# Revit family: Grohe_PlumbingFixture_Essentials_TowelRail_40366001a
name_source: partatom
category: Plumbing Fixtures
revit_build: Autodesk Revit 2018 (Build: 20190510_1515(x64)
units: mm (PartAtom-declared; Revit-internal decimal feet)

## family parameters
Cut with Voids When Loaded = No
Host = Face
OmniClass Number = 23.65.00.00
OmniClass Title = Supply and Distribution of Liquids and Gases
Part Type = Normal
Room Calculation Point = No
Round Connector Dimension = Use Diameter
Shared = No

## types (1)
- 40366001
    ADACompliant = No
    Assembly Code = D2010
    AssetType = Fixed
    BIMObjectName = Grohe_PlumbingFixture_Essentials_TowelRail_40366001
    CWFU = 0
    ClassificationName = Uniclass 2015
    ClassificationValue = Pr_40_20_76_90
    ColdWaterConnectionDiameter = 10 mm  [stored 0.0328084 ft]
    Color = Chrome
    Cost = 0 $
    Default Elevation = 0 mm  [stored 0 ft]
    Description = To create your very own bathroom design blending harmonious style and user-friendly functionality has never been easier. Simply add a choice of our beautifully crafted GROHE Essentials accessories such as the slim yet sturdy 600mm towel rail – the perfect place to hang a bathroom towel. The rail has concealed fastenings and a durable, easy-care GROHE StarLight chrome finish that will sparkle for years. It’s also easy to fit – just follow the clear step-by-step instructions. Don’t forget to check out other products in the comprehensive collection such as the robe hook, toilet brush set, toilet paper holder and numerous towel rails and bath grips. Or for added ease and convenience why not try one of our complementary all-in-one sets? GROHE Essentials accessories – precision craftsmanship, highest quality materials and design that lasts!
    DocumentationCertificates = www.grohe.co.uk/
    DocumentationInstallationGuide = www.grohe.co.uk/
    DocumentationLiterature = www.grohe.co.uk/
    DocumentationMaintenance = www.grohe.co.uk/
    DocumentationTechnical = www.grohe.co.uk/
    DurationUnit = Years
    Ecojoy = No
    ExpectedLife = 0
    FaucetMaterial = Grohe-Chrome
    Features = material: metal 
654 mm (useable length 600 mm) 
concealed fastening 
GROHE StarLight chrome finish 
suitable for screwing (including screws and dowels) or gluing (glue 40 915 000 sold separately)
    HWFU = 0
    HotWaterConnectionDiameter = 10 mm  [stored 0.0328084 ft]
    IfcExportAs = IfcPipeFitting
    IfcExportType = IfcPipeFittingType
    Keynote = N13
    LowEmittingMaterial = No
    Manufacturer = Grohe
    ManufacturerName = Grohe
    MasterformatNumber = 01 52 19
    MasterformatTitle = Sanitary Facilities
    Model = ESSENTIALS
    ModelNumber = 40366001
    ModelReference = ESSENTIALS - TOWEL RAIL
    NBSDescription = Towel rails
    NBSObjectName = Grohe - Towel rails
    NBSReference = 45-35-72/372
    NominalDepth = 0 mm  [stored 0 ft]
    NominalHeight = 0 mm  [stored 0 ft]
    NominalLength = 0 mm  [stored 0 ft]
    ProductPageURL = https://www.grohe.co.uk
    ProductionYear = 2020
    Type Comments = TOWEL RAIL
    TypeName = ESSENTIALS - TOWEL RAIL
    URL = www.grohe.com
    WarrantyDurationLabor = 0
    WarrantyDurationParts = 0
    WarrantyDurationUnit = Years
    _BSBibleVersion = 16
    _BimSpecGuid = 0
    _CurrentRevision = 1
    _DistributedBy = www.bimstore.co
    _ObjectUserGuide = www.bimstore.co

note: [stored X ft] marks values corroborated as IEEE doubles in the binary element streams (Revit-internal decimal feet)

## geometry (parser evidence)
native form markers: Sweep x3
no freeform markers — native parametric forms only
